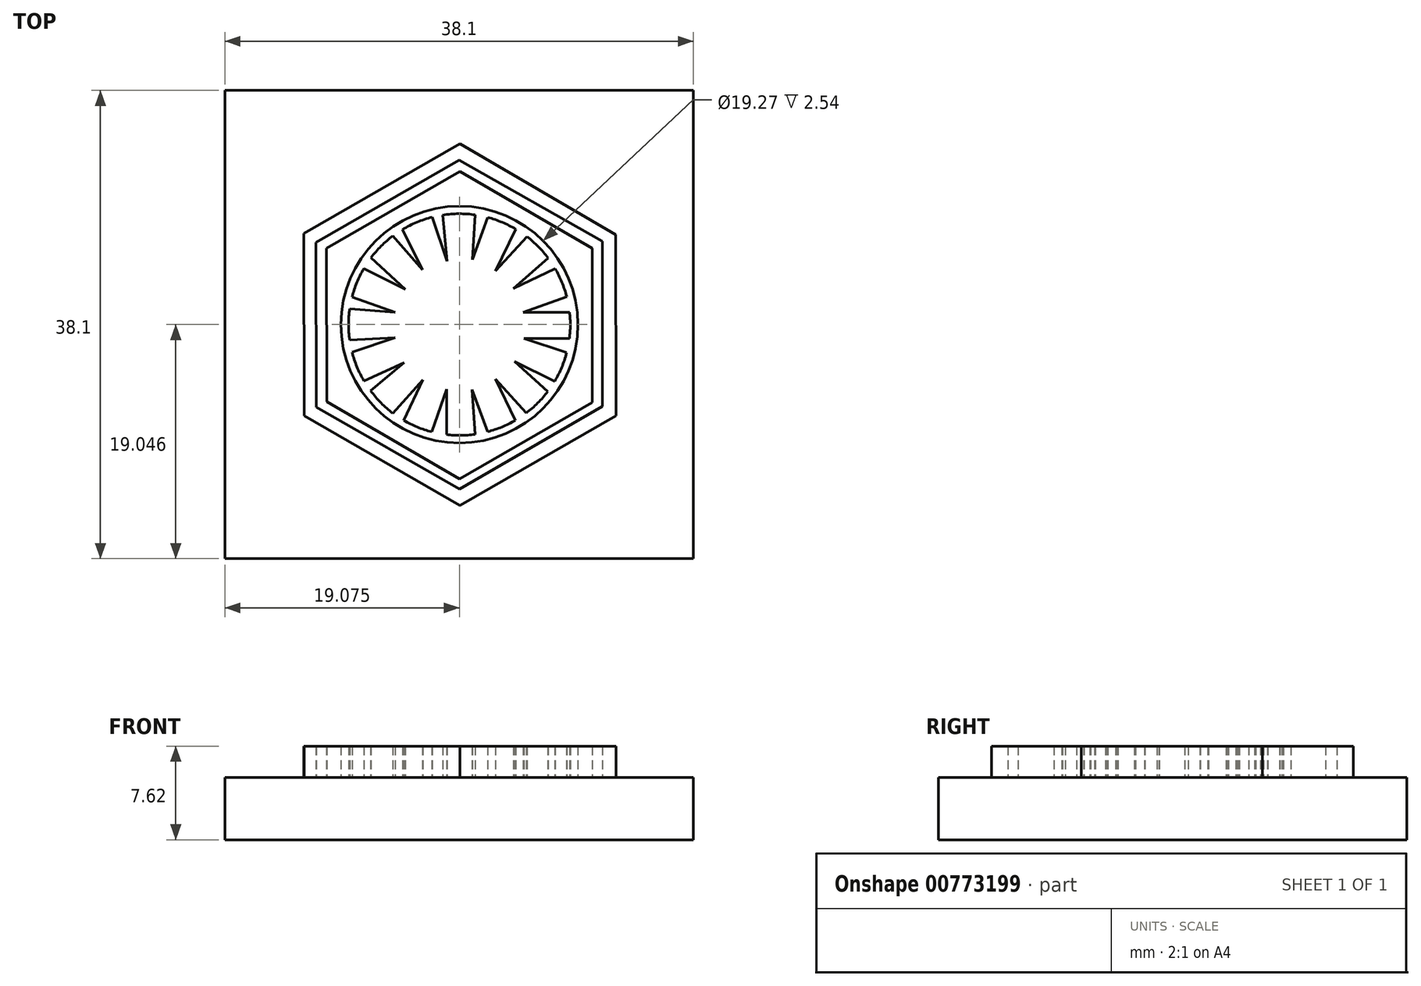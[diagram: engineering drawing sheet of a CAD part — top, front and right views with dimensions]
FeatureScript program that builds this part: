
annotation { "Feature Type Name" : "Feature", "Feature Type Description" : "" }
export const myFeature = defineFeature(function(context is Context, id is Id, definition is map)
    precondition{}
    {
        {
            var Q0;
            Q0=qCreatedBy(makeId("Top.planeOp"),FACE);
            var sketch = newSketch(context, id + "F0", { "sketchPlane" : qUnion([Q0])});
            skLineSegment(sketch, "E0.bottom", {"start": v(-23.39, 14.55) * mm, "end": v(14.71, 14.55) * mm});
            skLineSegment(sketch, "E0.top", {"start": v(-23.39, -23.55) * mm, "end": v(14.71, -23.55) * mm});
            skLineSegment(sketch, "E0.left", {"start": v(-23.39, 14.55) * mm, "end": v(-23.39, -23.55) * mm});
            skLineSegment(sketch, "E0.right", {"start": v(14.71, 14.55) * mm, "end": v(14.71, -23.55) * mm});
            skSolve(sketch);
        }
        {
            var Q0;
            Q0 = qSketchRegion(id + "F0", true);
            extrude(context, id + "F1", {"entities" : qUnion([Q0]), "depth" : 5.08 * mm, "offsetDistance" : 25.4 * mm});
        }
        {
            var Q0;
            Q0=makeQuery(id+"F1.opExtrude","CAP_FACE",FACE,{"disambiguationData":[OSD([sQuery(id+"F0.wireOp",EDGE,"E0.bottom"),sQuery(id+"F0.wireOp",EDGE,"E0.top"),sQuery(id+"F0.wireOp",EDGE,"E0.left"),sQuery(id+"F0.wireOp",EDGE,"E0.right")])],"isStart":false});
            var sketch = newSketch(context, id + "F2", { "sketchPlane" : qUnion([Q0])});
            skCircle(sketch, "E1", {"center": v(-4.32, -4.5) * mm, "radius": 9.02 * mm});
            skCircle(sketch, "E2", {"center": v(-4.32, -4.5) * mm, "radius": 9.64 * mm});
            skLineSegment(sketch, "E3", {"start": v(-15.1, -10.77) * mm, "end": v(-4.31, -17.07) * mm});
            skLineSegment(sketch, "E4", {"start": v(-4.31, -17.07) * mm, "end": v(6.48, -10.84) * mm});
            skLineSegment(sketch, "E5", {"start": v(6.48, -10.84) * mm, "end": v(6.48, 1.71) * mm});
            skLineSegment(sketch, "E6", {"start": v(6.48, 1.71) * mm, "end": v(-4.28, 7.96) * mm});
            skLineSegment(sketch, "E7", {"start": v(-4.28, 7.96) * mm, "end": v(-15.13, 1.7) * mm});
            skLineSegment(sketch, "E8", {"start": v(-15.13, 1.7) * mm, "end": v(-15.1, -10.77) * mm});
            skLineSegment(sketch, "E9", {"start": v(-15.97, -11.23) * mm, "end": v(-16, 2.17) * mm});
            skLineSegment(sketch, "E10", {"start": v(-16, 2.17) * mm, "end": v(-4.33, 8.9) * mm});
            skLineSegment(sketch, "E11", {"start": v(-4.33, 8.9) * mm, "end": v(7.3, 2.28) * mm});
            skLineSegment(sketch, "E12", {"start": v(7.3, 2.28) * mm, "end": v(7.33, -11.17) * mm});
            skLineSegment(sketch, "E13", {"start": v(7.33, -11.17) * mm, "end": v(-4.31, -17.88) * mm});
            skLineSegment(sketch, "E14", {"start": v(-4.31, -17.88) * mm, "end": v(-15.97, -11.23) * mm});
            skLineSegment(sketch, "E15", {"start": v(-16.93, -11.9) * mm, "end": v(-16.96, 2.9) * mm});
            skLineSegment(sketch, "E16", {"start": v(-16.96, 2.9) * mm, "end": v(-4.28, 10.22) * mm});
            skLineSegment(sketch, "E17", {"start": v(-4.28, 10.22) * mm, "end": v(8.4, 2.83) * mm});
            skLineSegment(sketch, "E18", {"start": v(8.4, 2.83) * mm, "end": v(8.42, -11.9) * mm});
            skLineSegment(sketch, "E19", {"start": v(8.42, -11.9) * mm, "end": v(-4.28, -19.23) * mm});
            skLineSegment(sketch, "E20", {"start": v(-4.28, -19.23) * mm, "end": v(-16.93, -11.9) * mm});
            skLineSegment(sketch, "E21", {"start": v(-11.54, -9.9) * mm, "end": v(-8.82, -7.6) * mm});
            skLineSegment(sketch, "E22", {"start": v(-8.82, -7.6) * mm, "end": v(-12.08, -9.09) * mm});
            skLineSegment(sketch, "E23", {"start": v(-13.05, -6.74) * mm, "end": v(-9.54, -5.57) * mm});
            skLineSegment(sketch, "E24", {"start": v(-9.54, -5.57) * mm, "end": v(-13.24, -5.78) * mm});
            skLineSegment(sketch, "E25", {"start": v(-13.24, -3.23) * mm, "end": v(-9.54, -3.5) * mm});
            skLineSegment(sketch, "E26", {"start": v(-9.54, -3.5) * mm, "end": v(-13.05, -2.26) * mm});
            skLineSegment(sketch, "E27", {"start": v(-12.1, 0.04) * mm, "end": v(-8.72, -1.64) * mm});
            skLineSegment(sketch, "E28", {"start": v(-8.72, -1.64) * mm, "end": v(-11.51, 0.93) * mm});
            skLineSegment(sketch, "E29", {"start": v(-9.72, -11.72) * mm, "end": v(-7.3, -9) * mm});
            skLineSegment(sketch, "E30", {"start": v(-7.3, -9) * mm, "end": v(-8.85, -12.3) * mm});
            skLineSegment(sketch, "E31", {"start": v(-6.56, -13.24) * mm, "end": v(-5.37, -9.77) * mm});
            skLineSegment(sketch, "E32", {"start": v(-5.37, -9.77) * mm, "end": v(-5.37, -13.46) * mm});
            skLineSegment(sketch, "E33", {"start": v(-3.05, -13.43) * mm, "end": v(-3.3, -9.8) * mm});
            skLineSegment(sketch, "E34", {"start": v(-3.3, -9.8) * mm, "end": v(-2.02, -13.22) * mm});
            skLineSegment(sketch, "E35", {"start": v(-9.73, 2.7) * mm, "end": v(-7.33, -0.03) * mm});
            skLineSegment(sketch, "E36", {"start": v(-7.33, -0.03) * mm, "end": v(-8.95, 3.23) * mm});
            skLineSegment(sketch, "E37", {"start": v(-6.53, 4.24) * mm, "end": v(-5.32, 0.64) * mm});
            skLineSegment(sketch, "E38", {"start": v(-5.32, 0.64) * mm, "end": v(-5.67, 4.41) * mm});
            skLineSegment(sketch, "E39", {"start": v(-3.26, 0.79) * mm, "end": v(-3.03, 4.42) * mm});
            skLineSegment(sketch, "E40", {"start": v(-3.26, 0.79) * mm, "end": v(-2, 4.21) * mm});
            skLineSegment(sketch, "E41", {"start": v(0.27, 3.26) * mm, "end": v(-1.38, -0.14) * mm});
            skLineSegment(sketch, "E42", {"start": v(-1.38, -0.14) * mm, "end": v(1.19, 2.64) * mm});
            skLineSegment(sketch, "E43", {"start": v(2.9, 0.9) * mm, "end": v(0.09, -1.58) * mm});
            skLineSegment(sketch, "E44", {"start": v(0.09, -1.58) * mm, "end": v(3.47, 0.05) * mm});
            skLineSegment(sketch, "E45", {"start": v(4.41, -2.23) * mm, "end": v(0.87, -3.51) * mm});
            skLineSegment(sketch, "E46", {"start": v(0.87, -3.51) * mm, "end": v(4.65, -3.51) * mm});
            skLineSegment(sketch, "E47", {"start": v(0.24, -12.29) * mm, "end": v(-1.38, -8.95) * mm});
            skLineSegment(sketch, "E48", {"start": v(-1.38, -8.95) * mm, "end": v(1.1, -11.7) * mm});
            skLineSegment(sketch, "E49", {"start": v(2.88, -9.94) * mm, "end": v(0.18, -7.52) * mm});
            skLineSegment(sketch, "E50", {"start": v(0.18, -7.52) * mm, "end": v(3.43, -9.12) * mm});
            skLineSegment(sketch, "E51", {"start": v(4.4, -6.8) * mm, "end": v(0.94, -5.62) * mm});
            skLineSegment(sketch, "E52", {"start": v(0.94, -5.62) * mm, "end": v(4.63, -5.62) * mm});
            skSolve(sketch);
        }
        {
            var Q0;
            Q0 = qSketchRegion(id + "F2", true);
            var Q1;
            Q1=makeQuery(id+"F2.imprint","IMPRINT",FACE,{"disambiguationData":[TD([[makeQuery(id+"F2.imprint","IMPRINT",EDGE,{"derivedFrom":sQuery(id+"F2.wireOp",EDGE,"E2")}),-1.0]])]});
            var Q2;
            {var subQ14=sQuery(id+"F2.wireOp",EDGE,"E21");Q2=makeQuery(id+"F2.imprint","IMPRINT",FACE,{"disambiguationData":[TD([[makeQuery(id+"F2.imprint","IMPRINT",EDGE,{"derivedFrom":subQ14}),-1.0]])]});}
            extrude(context, id + "F3", {"entities" : qUnion([Q0, Q1, Q2]), "operationType" : NewBodyOperationType.ADD, "depth" : 2.54 * mm, "offsetDistance" : 25.4 * mm});
        }
    });
